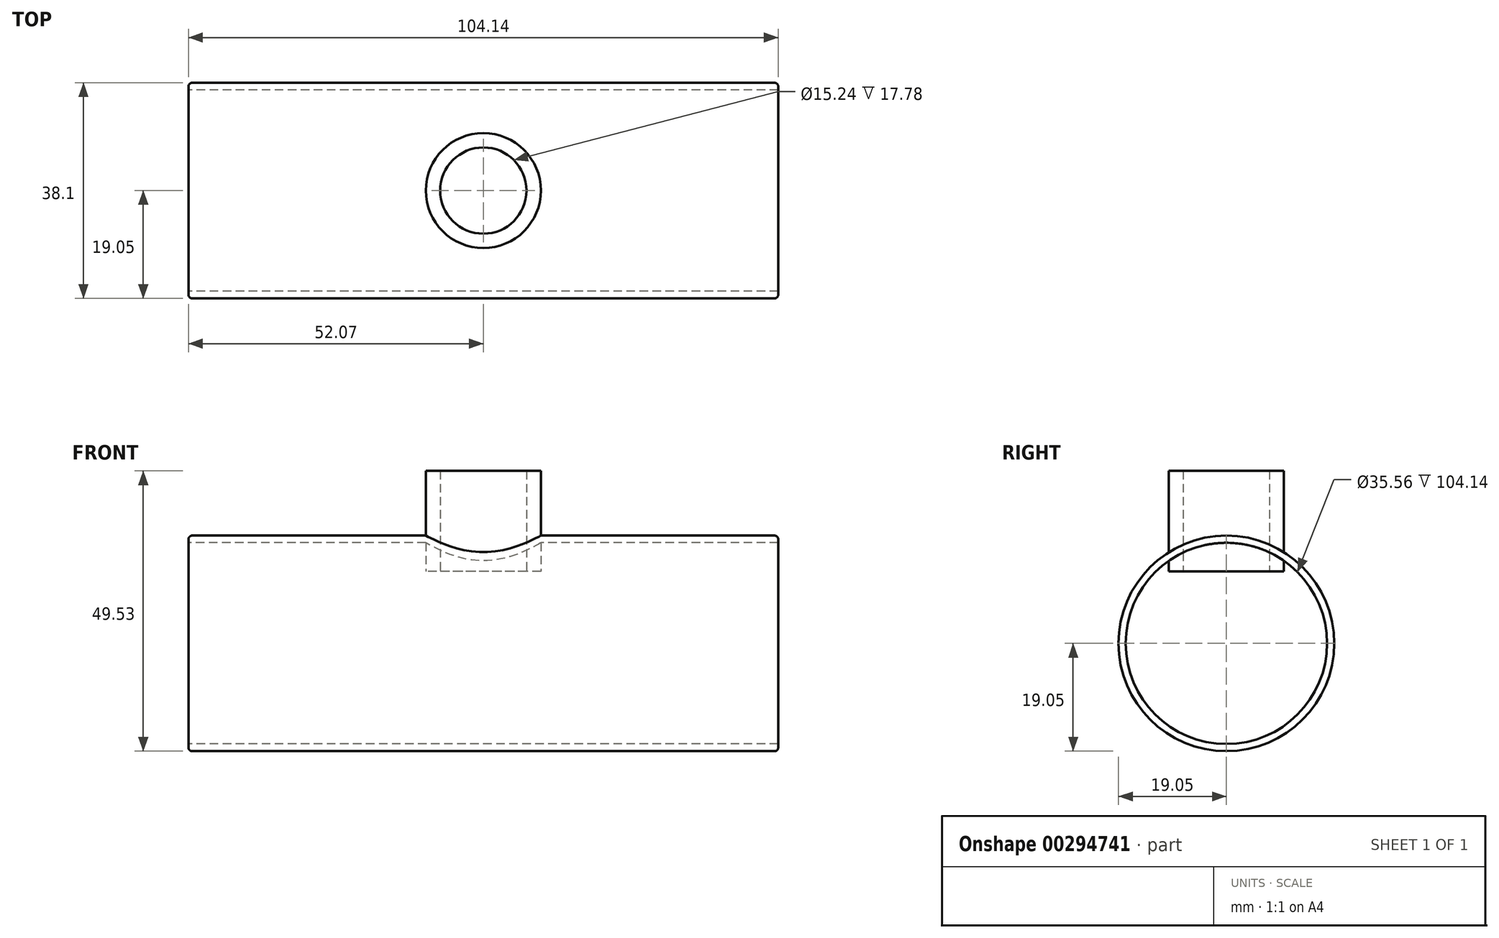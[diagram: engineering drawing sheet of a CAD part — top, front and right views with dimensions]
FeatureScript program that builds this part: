
annotation { "Feature Type Name" : "Feature", "Feature Type Description" : "" }
export const myFeature = defineFeature(function(context is Context, id is Id, definition is map)
    precondition{}
    {
        {
            var Q0;
            Q0=qCreatedBy(makeId("Right.planeOp"),FACE);
            var sketch = newSketch(context, id + "F0", { "sketchPlane" : qUnion([Q0])});
            skCircle(sketch, "E0", {"center": v(0, 0) * mm, "radius": 17.78 * mm});
            skCircle(sketch, "E1", {"center": v(0, 0) * mm, "radius": 19.05 * mm});
            skSolve(sketch);
        }
        {
            var Q0;
            Q0=qSketchRegion(id+"F0",true);
            extrude(context, id + "F1", {"entities" : qUnion([Q0]), "endBound" : BoundingType.SYMMETRIC, "depth" : 104.14 * mm});
        }
        {
            var Q0;
            Q0=makeQuery(id+"F1.opExtrude","CAP_EDGE",EDGE,{"disambiguationData":[OSD([sQuery(id+"F0.wireOp",EDGE,"E1")])],"isStart":false});
            var Q1;
            Q1=makeQuery(id+"F1.opExtrude","CAP_EDGE",EDGE,{"disambiguationData":[OSD([sQuery(id+"F0.wireOp",EDGE,"E1")])],"isStart":true});
            fillet(context, id + "F2", {"entities" : qUnion([Q0, Q1]), "radius" : 0.64 * mm, "tangentPropagation" : true, "allowEdgeOverflow" : false});
        }
        {
            var Q0;
            Q0=qCreatedBy(makeId("Top.planeOp"),FACE);
            var sketch = newSketch(context, id + "F3", { "sketchPlane" : qUnion([Q0])});
            skCircle(sketch, "E2", {"center": v(0, 0) * mm, "radius": 10.16 * mm});
            skCircle(sketch, "E3", {"center": v(0, 0) * mm, "radius": 7.62 * mm});
            skSolve(sketch);
        }
        {
            var Q0;
            Q0=qSketchRegion(id+"F3",true);
            extrude(context, id + "F4", {"entities" : qUnion([Q0]), "operationType" : NewBodyOperationType.ADD, "depth" : 30.48 * mm});
        }
        {
            var Q0;
            Q0=qCreatedBy(makeId("Top.planeOp"),FACE);
            var sketch = newSketch(context, id + "F5", { "sketchPlane" : qUnion([Q0])});
            skCircle(sketch, "E4", {"center": v(0, 0) * mm, "radius": 7.62 * mm});
            skSolve(sketch);
        }
        {
            var Q0;
            Q0=qSketchRegion(id+"F5",true);
            extrude(context, id + "F6", {"entities" : qUnion([Q0]), "operationType" : NewBodyOperationType.REMOVE, "endBound" : BoundingType.THROUGH_ALL, "depth" : 5.08 * mm});
        }
        {
            var Q0;
            Q0=qCreatedBy(makeId("Right.planeOp"),FACE);
            var sketch = newSketch(context, id + "F7", { "sketchPlane" : qUnion([Q0])});
            skArc(sketch, "E5", {"start": v(-10.16, 14.6) * mm, "mid": v(0, -17.78) * mm, "end": v(10.16, 14.6) * mm});
            skLineSegment(sketch, "E6", {"start": v(-10.16, 12.7) * mm, "end": v(10.16, 12.7) * mm});
            skLineSegment(sketch, "E7", {"start": v(-10.16, 14.6) * mm, "end": v(-10.16, 12.7) * mm});
            skLineSegment(sketch, "E8", {"start": v(10.16, 12.7) * mm, "end": v(10.16, 14.6) * mm});
            skPoint(sketch, "E9.MirrorCS.end.orphan", {"position": v(10.16, 0) * mm});
            skSolve(sketch);
        }
        {
            var Q0;
            Q0=qSketchRegion(id+"F7",true);
            extrude(context, id + "F8", {"entities" : qUnion([Q0]), "operationType" : NewBodyOperationType.REMOVE, "endBound" : BoundingType.SYMMETRIC, "depth" : 50.8 * mm});
        }
    });
